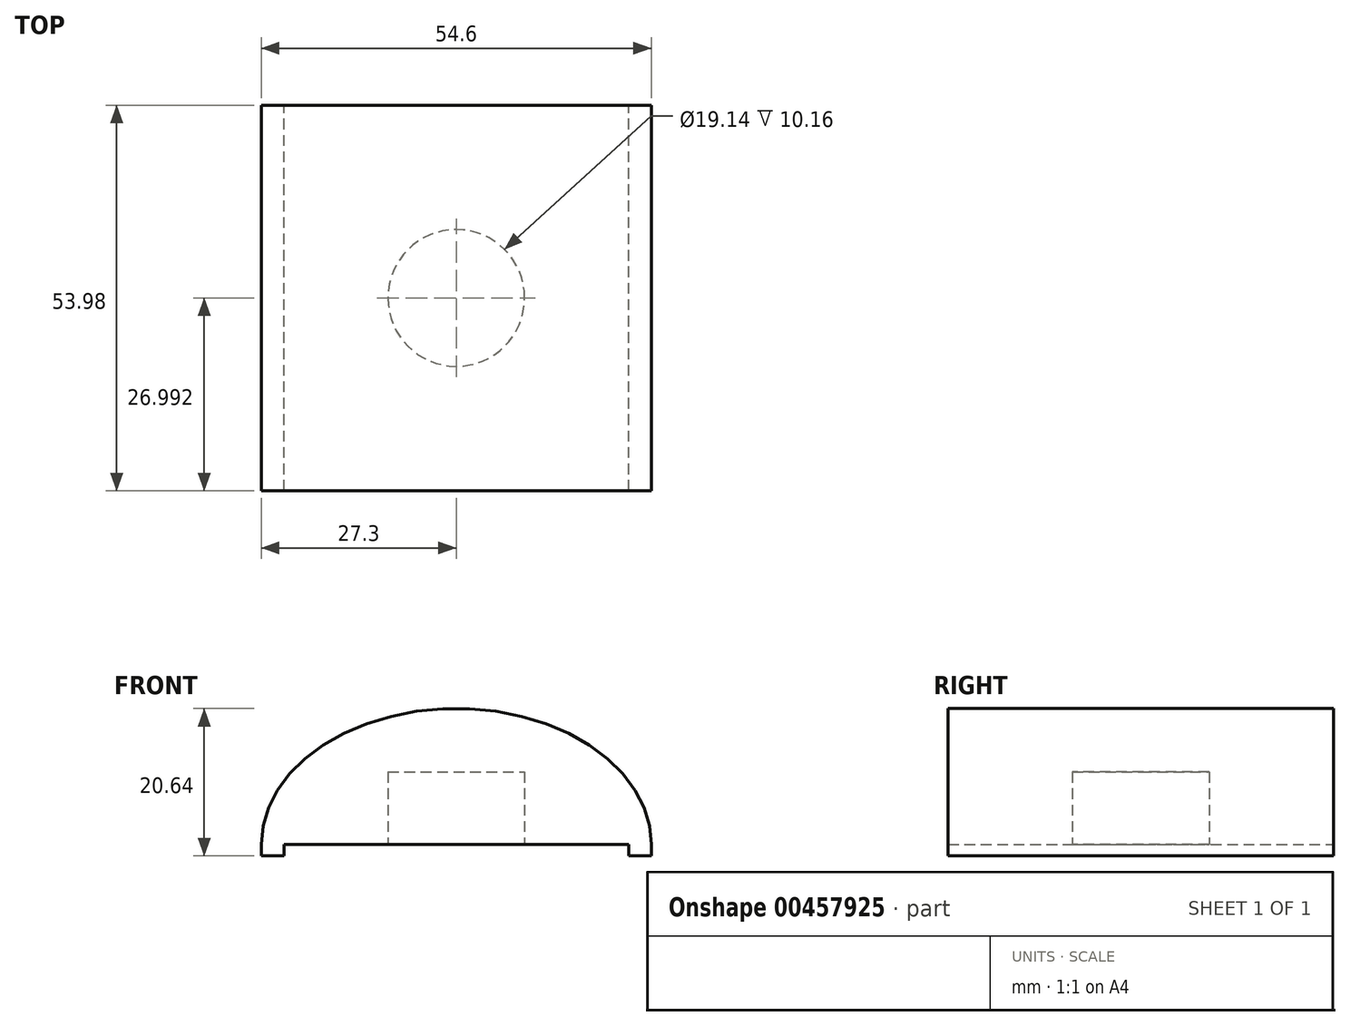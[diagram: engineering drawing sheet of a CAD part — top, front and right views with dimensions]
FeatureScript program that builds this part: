
annotation { "Feature Type Name" : "Feature", "Feature Type Description" : "" }
export const myFeature = defineFeature(function(context is Context, id is Id, definition is map)
    precondition{}
    {
        {
            var Q0;
            Q0=qCreatedBy(makeId("Front.planeOp"),FACE);
            var sketch = newSketch(context, id + "F0", { "sketchPlane" : qUnion([Q0])});
            skEllipticalArc(sketch, "E0", {});
            skLineSegment(sketch, "E1", {"start": v(-24.13, 0) * mm, "end": v(24.12, 0) * mm});
            skLineSegment(sketch, "E2.top", {"start": v(-27.3, -1.59) * mm, "end": v(-24.13, -1.59) * mm});
            skLineSegment(sketch, "E2.left", {"start": v(-27.3, 0) * mm, "end": v(-27.3, -1.59) * mm});
            skLineSegment(sketch, "E2.right", {"start": v(-24.13, 0) * mm, "end": v(-24.13, -1.59) * mm});
            skLineSegment(sketch, "E3.top", {"start": v(27.3, -1.59) * mm, "end": v(24.12, -1.59) * mm});
            skLineSegment(sketch, "E3.left", {"start": v(27.3, 0) * mm, "end": v(27.3, -1.59) * mm});
            skLineSegment(sketch, "E3.right", {"start": v(24.12, 0) * mm, "end": v(24.12, -1.59) * mm});
            const initialGuessF0  = {"E0": [0, 0, 1, 0, 0.027305, 0.01905, 0, 3.141592653589793]};
            skSetInitialGuess(sketch, initialGuessF0);
            skSolve(sketch);
        }
        {
            var Q0;
            Q0=makeQuery(id+"F0.imprint","IMPRINT",FACE,{"disambiguationData":[TD([[makeQuery(id+"F0.imprint","IMPRINT",EDGE,{"derivedFrom":sQuery(id+"F0.wireOp",EDGE,"E0")}),1.0]])]});
            extrude(context, id + "F1", {"entities" : qUnion([Q0]), "depth" : 53.97 * mm});
        }
        {
            var Q0;
            Q0=makeQuery(id+"F1.opExtrude","SWEPT_FACE",FACE,{"disambiguationData":[OSD([sQuery(id+"F0.wireOp",EDGE,"E1")])]});
            var sketch = newSketch(context, id + "F2", { "sketchPlane" : qUnion([Q0])});
            skLineSegment(sketch, "E4", {"start": v(24.12, 26.99) * mm, "end": v(-24.13, 26.99) * mm, "construction": true});
            skCircle(sketch, "E5", {"center": v(0, 26.99) * mm, "radius": 9.65 * mm, "construction": true});
            skCircle(sketch, "E6", {"center": v(0, 26.99) * mm, "radius": 9.57 * mm});
            skSolve(sketch);
        }
        {
            var Q0;
            Q0=makeQuery(id+"F2.imprint","IMPRINT",FACE,{"disambiguationData":[TD([[makeQuery(id+"F2.imprint","IMPRINT",EDGE,{"derivedFrom":sQuery(id+"F2.wireOp",EDGE,"E6")}),1.0]])]});
            extrude(context, id + "F3", {"entities" : qUnion([Q0]), "operationType" : NewBodyOperationType.REMOVE, "oppositeDirection" : true, "depth" : 10.16 * mm});
        }
    });
